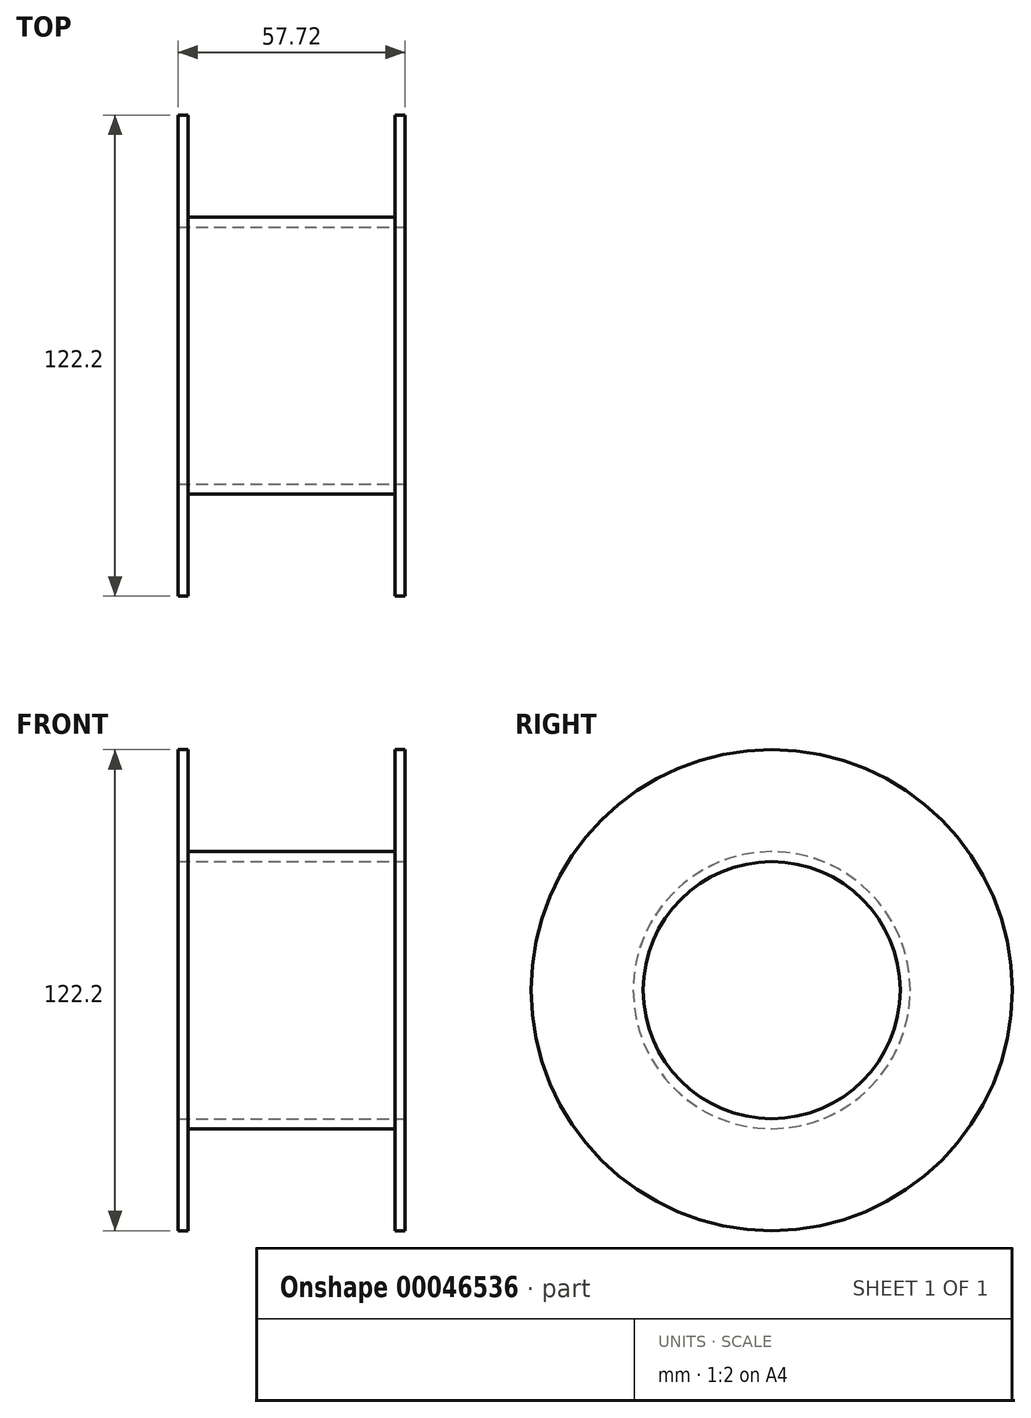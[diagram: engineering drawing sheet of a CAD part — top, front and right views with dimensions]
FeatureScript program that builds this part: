
annotation { "Feature Type Name" : "Feature", "Feature Type Description" : "" }
export const myFeature = defineFeature(function(context is Context, id is Id, definition is map)
    precondition{}
    {
        {
            var Q0;
            Q0=qCreatedBy(makeId("Front.planeOp"),FACE);
            var sketch = newSketch(context, id + "F0", { "sketchPlane" : qUnion([Q0])});
            skLineSegment(sketch, "E0.rect.bottom", {"start": v(-28.86, 14.23) * mm, "end": v(28.86, 14.23) * mm});
            skLineSegment(sketch, "E0.rect.top", {"start": v(-28.86, -14.23) * mm, "end": v(28.86, -14.23) * mm});
            skLineSegment(sketch, "E0.rect.left", {"start": v(-28.86, 14.23) * mm, "end": v(-28.86, -14.23) * mm});
            skLineSegment(sketch, "E0.rect.right", {"start": v(28.86, 14.23) * mm, "end": v(28.86, -14.23) * mm});
            skPoint(sketch, "E0.rect.middle", {"position": v(0, 0) * mm});
            skSolve(sketch);
        }
        {
            var Q0;
            Q0=qCreatedBy(makeId("Right.planeOp"),FACE);
            var sketch = newSketch(context, id + "F1", { "sketchPlane" : qUnion([Q0])});
            skPoint(sketch, "E1.1.internal.orphan", {"position": v(79.3, 0) * mm});
            skPoint(sketch, "E1.4.internal.orphan", {"position": v(0, 73.35) * mm});
            skPoint(sketch, "E2.first.point", {"position": v(0, 0) * mm});
            skPoint(sketch, "E2.second.point", {"position": v(0, 91.3) * mm});
            skPoint(sketch, "E2.third.point", {"position": v(-31.67, 78.9) * mm});
            skPoint(sketch, "E3.end.orphan", {"position": v(0, 110.03) * mm});
            skCircle(sketch, "E4", {"center": v(0, 46.87) * mm, "radius": 46.87 * mm});
            skSolve(sketch);
        }
        {
            var Q0;
            Q0 = qSketchRegion(id + "F0", true);
            var Q1;
            Q1 = qConstructionFilter(qBodyType(qCreatedBy(id + "F1" ,EDGE), BodyType.WIRE), ConstructionObject.NO);
            sweep(context, id + "F2", {"profiles" : qUnion([Q0]), "path" : qUnion([Q1])});
        }
        {
            var Q0;
            Q0=makeQuery(id+"F2.opSweep","SWEPT_FACE",FACE,{"disambiguationData":[OSD([sQuery(id+"F0.wireOp",EDGE,"E0.rect.top"),sQuery(id+"F1.wireOp",EDGE,"E4")])]});
            shell(context, id + "F3", {"entities" : qUnion([Q0]), "thickness" : 2.54 * mm});
        }
    });
